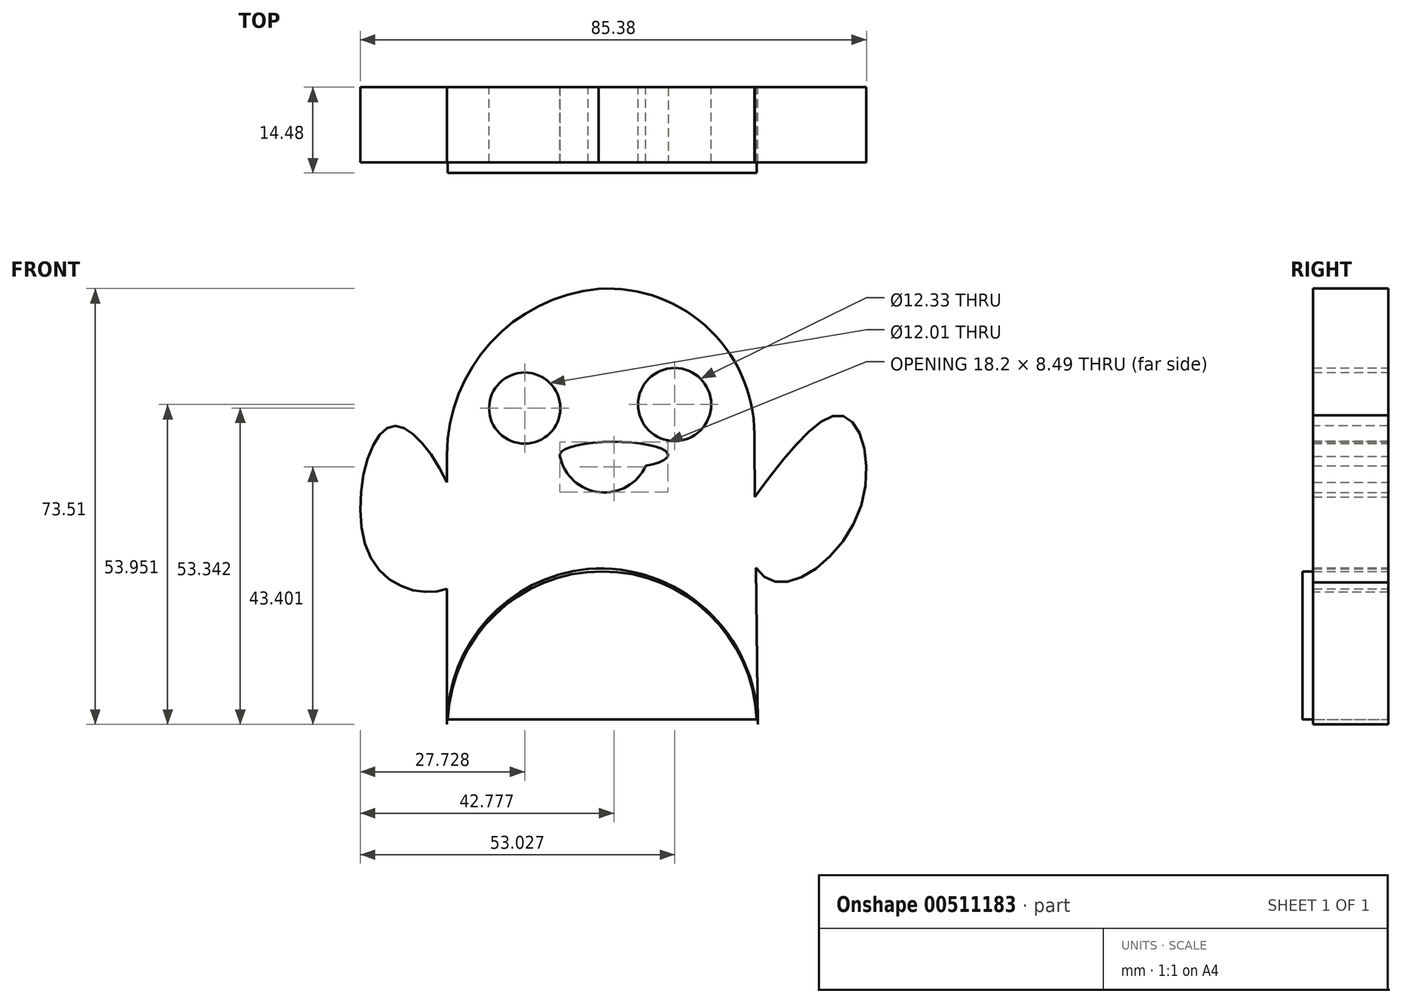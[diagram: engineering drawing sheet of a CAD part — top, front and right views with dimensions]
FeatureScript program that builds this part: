
annotation { "Feature Type Name" : "Feature", "Feature Type Description" : "" }
export const myFeature = defineFeature(function(context is Context, id is Id, definition is map)
    precondition{}
    {
        {
            var Q0;
            Q0=qCreatedBy(makeId("Front.planeOp"),FACE);
            var sketch = newSketch(context, id + "F0", { "sketchPlane" : qUnion([Q0])});
            skLineSegment(sketch, "E0", {"start": v(-33.53, 8.69) * mm, "end": v(-33.53, -36.73) * mm});
            skLineSegment(sketch, "E1", {"start": v(-5.06, -36.73) * mm, "end": v(18.9, -36.73) * mm});
            skLineSegment(sketch, "E2", {"start": v(-33.53, -36.73) * mm, "end": v(-5.06, -36.73) * mm});
            skArc(sketch, "E3", {"start": v(-7.92, 36.73) * mm, "mid": v(-26.16, 27.67) * mm, "end": v(-33.53, 8.69) * mm});
            skArc(sketch, "E4", {"start": v(18.3, 10.85) * mm, "mid": v(10.97, 29.65) * mm, "end": v(-7.92, 36.73) * mm});
            skLineSegment(sketch, "E5", {"start": v(18.3, 10.85) * mm, "end": v(18.9, -36.73) * mm});
            skCircle(sketch, "E6", {"center": v(-20.42, 16.61) * mm, "radius": 6 * mm});
            skCircle(sketch, "E7", {"center": v(4.88, 17.22) * mm, "radius": 6.16 * mm});
            skEllipse(sketch, "E8", {"center": v(-5.37, 8.69) * mm, "majorRadius": 9.14 * mm, "minorRadius": 2.24 * mm, "majorAxis": v(-1, 0)});
            skArc(sketch, "E9", {"start": v(-9.75, -10.52) * mm, "mid": v(-26.7, -19.03) * mm, "end": v(-33.53, -36.73) * mm});
            skArc(sketch, "E10", {"start": v(18.9, -36.73) * mm, "mid": v(10.25, -17.42) * mm, "end": v(-9.75, -10.52) * mm});
            skArc(sketch, "E11", {"start": v(-33.53, 0) * mm, "mid": v(-45.34, -7.01) * mm, "end": v(-33.53, -14.02) * mm});
            skArc(sketch, "E12", {"start": v(18.57, -10.52) * mm, "mid": v(30.18, -6.56) * mm, "end": v(18.48, -2.9) * mm});
            skArc(sketch, "E13", {"start": v(-14.51, 8.69) * mm, "mid": v(-7.92, 2.44) * mm, "end": v(0, 6.87) * mm});
            skSolve(sketch);
        }
        {
            var Q0;
            {var subQ6=sQuery(id+"F0.wireOp",EDGE,"E3");Q0=makeQuery(id+"F0.imprint","IMPRINT",FACE,{"disambiguationData":[TD([[makeQuery(id+"F0.imprint","IMPRINT",EDGE,{"derivedFrom":subQ6}),1.0]])]});}
            extrude(context, id + "F1", {"entities" : qUnion([Q0]), "depth" : 12.7 * mm, "offsetDistance" : 25.4 * mm});
        }
        {
            var Q0;
            Q0=qCreatedBy(makeId("Front.planeOp"),FACE);
            var sketch = newSketch(context, id + "F2", { "sketchPlane" : qUnion([Q0])});
            skLineSegment(sketch, "E14", {"start": v(-33.4, -35.89) * mm, "end": v(18.73, -35.89) * mm});
            skArc(sketch, "E15", {"start": v(18.73, -35.89) * mm, "mid": v(-7.33, -10.93) * mm, "end": v(-33.4, -35.89) * mm});
            skSolve(sketch);
        }
        {
            var Q0;
            Q0=makeQuery(id+"F2.imprint","IMPRINT",FACE,{"disambiguationData":[TD([[makeQuery(id+"F2.imprint","IMPRINT",EDGE,{"derivedFrom":sQuery(id+"F2.wireOp",EDGE,"E14")}),1.0]])]});
            extrude(context, id + "F3", {"entities" : qUnion([Q0]), "depth" : 14.48 * mm, "offsetDistance" : 25.4 * mm});
        }
        {
            var Q0;
            Q0=qCreatedBy(makeId("Front.planeOp"),FACE);
            var sketch = newSketch(context, id + "F4", { "sketchPlane" : qUnion([Q0])});
            skFitSpline(sketch, "E16", {"points": [v(19.81, 3.5) * mm, v(32.92, 15.4) * mm, v(36.27, 0) * mm, v(21.64, -12.65) * mm, v(16.46, -3.81) * mm, v(19.81, 3.5) * mm]});
            skFitSpline(sketch, "E17", {"points": [v(-31.8, 0) * mm, v(-43.22, 13.43) * mm, v(-46.3, -8.8) * mm, v(-32.72, -13.43) * mm, v(-31.8, 0) * mm]});
            skSolve(sketch);
        }
        {
            var Q0;
            Q0=makeQuery(id+"F4.imprint","IMPRINT",FACE,{"disambiguationData":[TD([[makeQuery(id+"F4.imprint","IMPRINT",EDGE,{"derivedFrom":sQuery(id+"F4.wireOp",EDGE,"E17")}),1.0]])]});
            var Q1;
            Q1=makeQuery(id+"F4.imprint","IMPRINT",FACE,{"disambiguationData":[TD([[makeQuery(id+"F4.imprint","IMPRINT",EDGE,{"derivedFrom":sQuery(id+"F4.wireOp",EDGE,"E16")}),-1.0]])]});
            extrude(context, id + "F5", {"entities" : qUnion([Q0, Q1]), "operationType" : NewBodyOperationType.ADD, "depth" : 12.7 * mm, "offsetDistance" : 25.4 * mm});
        }
    });
